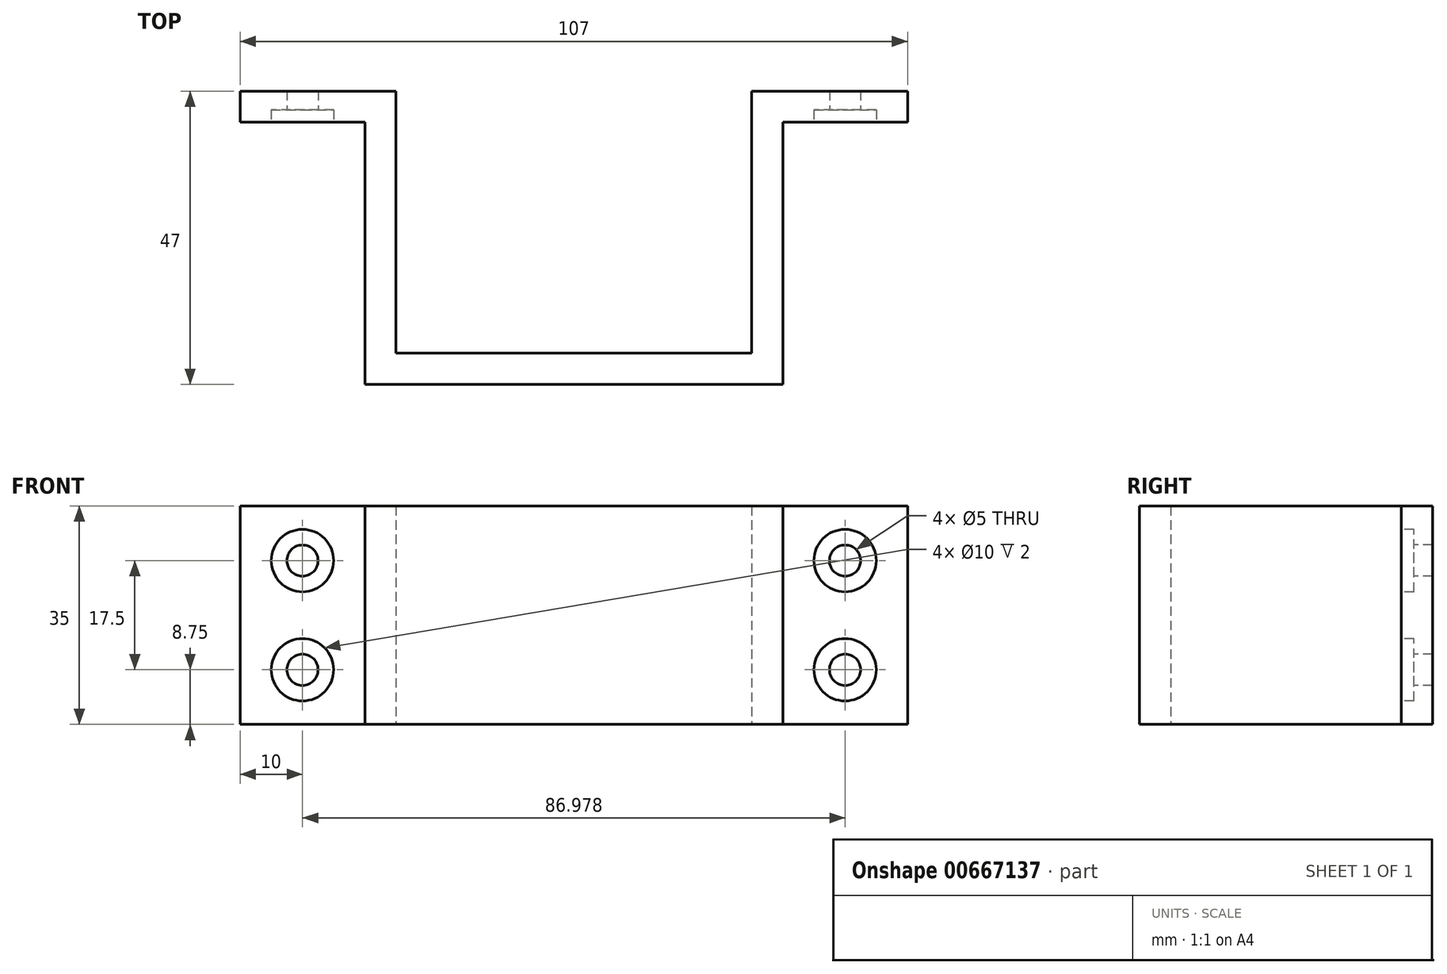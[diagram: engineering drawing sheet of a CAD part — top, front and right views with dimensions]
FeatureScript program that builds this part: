
annotation { "Feature Type Name" : "Feature", "Feature Type Description" : "" }
export const myFeature = defineFeature(function(context is Context, id is Id, definition is map)
    precondition{}
    {
        {
            var Q0;
            Q0=qCreatedBy(makeId("Top.planeOp"),FACE);
            var sketch = newSketch(context, id + "F0", { "sketchPlane" : qUnion([Q0])});
            skLineSegment(sketch, "E0.bottom", {"start": v(0, 0) * mm, "end": v(-20, 0) * mm});
            skLineSegment(sketch, "E0.top", {"start": v(0, 5) * mm, "end": v(-20, 5) * mm});
            skLineSegment(sketch, "E0.left", {"start": v(0, 0) * mm, "end": v(0, 5) * mm});
            skLineSegment(sketch, "E0.right", {"start": v(-20, 0) * mm, "end": v(-20, 5) * mm});
            skLineSegment(sketch, "E1.bottom", {"start": v(0, 5) * mm, "end": v(5, 5) * mm});
            skLineSegment(sketch, "E1.top", {"start": v(0, -37) * mm, "end": v(5, -37) * mm});
            skLineSegment(sketch, "E1.left", {"start": v(0, 5) * mm, "end": v(0, -37) * mm});
            skLineSegment(sketch, "E1.right", {"start": v(5, 5) * mm, "end": v(5, -37) * mm});
            skLineSegment(sketch, "E2.bottom", {"start": v(0, -37) * mm, "end": v(67, -37) * mm});
            skLineSegment(sketch, "E2.top", {"start": v(0, -42) * mm, "end": v(67, -42) * mm});
            skLineSegment(sketch, "E2.left", {"start": v(0, -37) * mm, "end": v(0, -42) * mm});
            skLineSegment(sketch, "E2.right", {"start": v(67, -37) * mm, "end": v(67, -42) * mm});
            skLineSegment(sketch, "E3.bottom", {"start": v(67, -37) * mm, "end": v(62, -37) * mm});
            skLineSegment(sketch, "E3.top", {"start": v(67, 5) * mm, "end": v(62, 5) * mm});
            skLineSegment(sketch, "E3.left", {"start": v(67, -37) * mm, "end": v(67, 5) * mm});
            skLineSegment(sketch, "E3.right", {"start": v(62, -37) * mm, "end": v(62, 5) * mm});
            skLineSegment(sketch, "E4.bottom", {"start": v(67, 5) * mm, "end": v(87, 5) * mm});
            skLineSegment(sketch, "E4.top", {"start": v(67, 0) * mm, "end": v(87, 0) * mm});
            skLineSegment(sketch, "E4.left", {"start": v(67, 5) * mm, "end": v(67, 0) * mm});
            skLineSegment(sketch, "E4.right", {"start": v(87, 5) * mm, "end": v(87, 0) * mm});
            skSolve(sketch);
        }
        {
            var Q0;
            Q0 = qSketchRegion(id + "F0", true);
            extrude(context, id + "F1", {"entities" : qUnion([Q0]), "depth" : 35 * mm, "offsetDistance" : 25 * mm});
        }
        {
            var Q0;
            Q0=makeQuery(id+"F1.opExtrude","SWEPT_FACE",FACE,{"disambiguationData":[OSD([sQuery(id+"F0.wireOp",EDGE,"E0.bottom")])]});
            var sketch = newSketch(context, id + "F2", { "sketchPlane" : qUnion([Q0])});
            skLineSegment(sketch, "E5", {"start": v(0, 0) * mm, "end": v(-20, 0) * mm});
            skCircle(sketch, "E6", {"center": v(-10, 8.75) * mm, "radius": 2.5 * mm});
            skCircle(sketch, "E7", {"center": v(-10, 26.25) * mm, "radius": 2.5 * mm});
            skLineSegment(sketch, "E8", {"start": v(76.98, 0) * mm, "end": v(76.98, 35) * mm});
            skCircle(sketch, "E9", {"center": v(76.98, 8.75) * mm, "radius": 2.5 * mm});
            skCircle(sketch, "E10", {"center": v(76.98, 26.25) * mm, "radius": 2.5 * mm});
            skSolve(sketch);
        }
        {
            var Q0;
            Q0=sQuery(id+"F2.wireOp",VERTEX,"E7.center");
            var Q1;
            Q1=sQuery(id+"F2.wireOp",VERTEX,"E6.center");
            var Q2;
            Q2=sQuery(id+"F2.wireOp",VERTEX,"E9.center");
            var Q3;
            Q3=sQuery(id+"F2.wireOp",VERTEX,"E10.center");
            var Q4;
            Q4=makeQuery(id+"F1.opExtrude","SWEPT_BODY",BODY,{"disambiguationData":[OSD([sQuery(id+"F0.wireOp",EDGE,"E0.bottom"),sQuery(id+"F0.wireOp",EDGE,"E0.top"),sQuery(id+"F0.wireOp",EDGE,"E0.right"),sQuery(id+"F0.wireOp",EDGE,"E1.bottom"),sQuery(id+"F0.wireOp",EDGE,"E1.left"),sQuery(id+"F0.wireOp",EDGE,"E1.right"),sQuery(id+"F0.wireOp",EDGE,"E2.bottom"),sQuery(id+"F0.wireOp",EDGE,"E2.top"),sQuery(id+"F0.wireOp",EDGE,"E2.left"),sQuery(id+"F0.wireOp",EDGE,"E2.right"),sQuery(id+"F0.wireOp",EDGE,"E3.top"),sQuery(id+"F0.wireOp",EDGE,"E3.left"),sQuery(id+"F0.wireOp",EDGE,"E3.right"),sQuery(id+"F0.wireOp",EDGE,"E4.bottom"),sQuery(id+"F0.wireOp",EDGE,"E4.top"),sQuery(id+"F0.wireOp",EDGE,"E4.right")])]});
            hole(context, id + "F3", {"style" : HoleStyle.C_BORE, "endStyle" : HoleEndStyle.BLIND, "holeDiameter" : 5 * mm, "cBoreDiameter" : 10 * mm, "cBoreDepth" : 2 * mm, "majorDiameter" : 5 * mm, "holeDepth" : 5 * mm, "isTappedThrough" : true, "tappedDepth" : 12 * mm, "tapClearance" : 3, "startFromSketch" : true, "locations" : qUnion([Q0, Q1, Q2, Q3]), "scope" : qUnion([Q4])});
        }
    });
